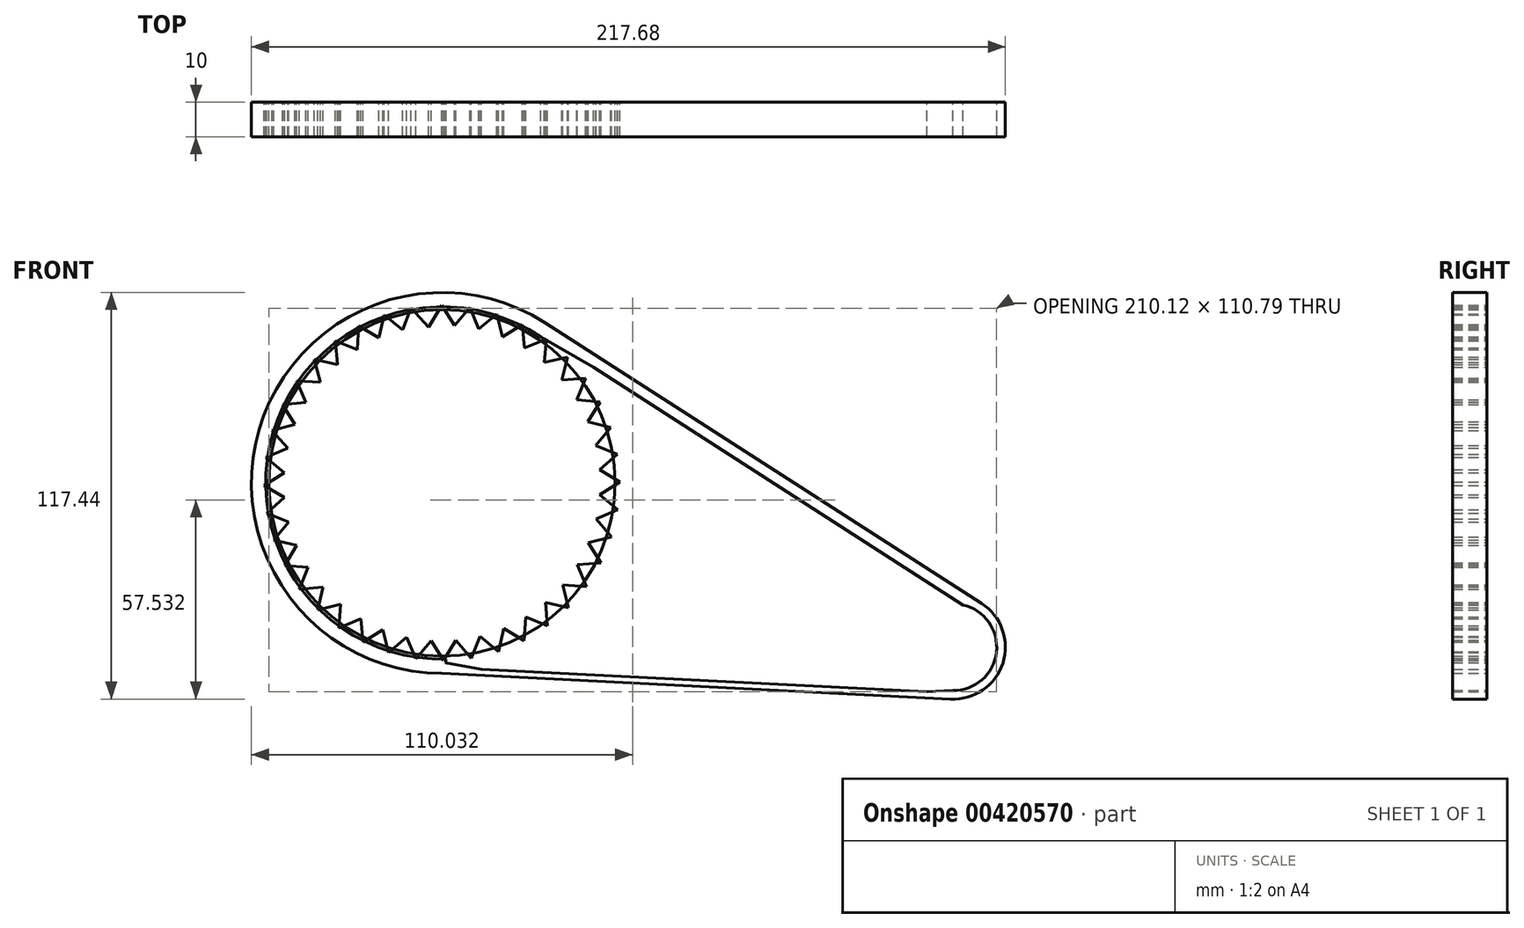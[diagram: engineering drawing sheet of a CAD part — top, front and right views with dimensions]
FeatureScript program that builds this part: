
annotation { "Feature Type Name" : "Feature", "Feature Type Description" : "" }
export const myFeature = defineFeature(function(context is Context, id is Id, definition is map)
    precondition{}
    {
        {
            var Q0;
            Q0=qCreatedBy(makeId("Front.planeOp"),FACE);
            var sketch = newSketch(context, id + "F0", { "sketchPlane" : qUnion([Q0])});
            skCircle(sketch, "E0", {"center": v(0, 0) * mm, "radius": 50 * mm});
            skSolve(sketch);
        }
        {
            var Q0;
            Q0=makeQuery(id+"F0.imprint","IMPRINT",FACE,{"disambiguationData":[TD([[makeQuery(id+"F0.imprint","IMPRINT",EDGE,{"derivedFrom":sQuery(id+"F0.wireOp",EDGE,"E0")}),1.0]])]});
            extrude(context, id + "F1", {"entities" : qUnion([Q0]), "depth" : 10 * mm});
        }
        {
            var Q0;
            Q0=qCreatedBy(makeId("Front.planeOp"),FACE);
            var sketch = newSketch(context, id + "F2", { "sketchPlane" : qUnion([Q0])});
            skCircle(sketch, "E1", {"center": v(147.68, -47.44) * mm, "radius": 12.5 * mm});
            skLineSegment(sketch, "E2", {"start": v(0, -55) * mm, "end": v(146.92, -62.42) * mm});
            skLineSegment(sketch, "E3", {"start": v(29.76, 46.26) * mm, "end": v(155.8, -34.82) * mm});
            skCircle(sketch, "E4", {"center": v(0, 0) * mm, "radius": 50.89 * mm});
            skLineSegment(sketch, "E5", {"start": v(29.76, 46.26) * mm, "end": v(0, -55) * mm});
            skCircle(sketch, "E6", {"center": v(0, 0) * mm, "radius": 55 * mm});
            skCircle(sketch, "E7", {"center": v(147.68, -47.44) * mm, "radius": 15 * mm});
            skLineSegment(sketch, "E8", {"start": v(43.69, 33.41) * mm, "end": v(146.17, -32.52) * mm});
            skLineSegment(sketch, "E9", {"start": v(139.96, -60.3) * mm, "end": v(11.38, -53.81) * mm});
            skLineSegment(sketch, "E10", {"start": v(43.69, 33.41) * mm, "end": v(28.58, 42.24) * mm});
            skLineSegment(sketch, "E11", {"start": v(11.38, -53.81) * mm, "end": v(0.91, -51.9) * mm});
            skLineSegment(sketch, "E12", {"start": v(146.17, -32.52) * mm, "end": v(150.4, -35.24) * mm});
            skLineSegment(sketch, "E13", {"start": v(139.96, -60.3) * mm, "end": v(149.06, -59.86) * mm});
            skSolve(sketch);
        }
        {
            var Q0;
            Q0 = qSketchRegion(id + "F2", true);
            extrude(context, id + "F3", {"entities" : qUnion([Q0]), "operationType" : NewBodyOperationType.ADD, "depth" : 10 * mm});
        }
        {
            var Q0;
            Q0=qCreatedBy(makeId("Front.planeOp"),FACE);
            var sketch = newSketch(context, id + "F4", { "sketchPlane" : qUnion([Q0])});
            skLineSegment(sketch, "E14", {"start": v(-4.25, 44.43) * mm, "end": v(0, 51.33) * mm});
            skLineSegment(sketch, "E15.MirrorCS", {"start": v(4.25, 44.43) * mm, "end": v(0, 51.33) * mm});
            skLineSegment(sketch, "E16.1.0", {"start": v(2.73, 44.54) * mm, "end": v(8, 50.7) * mm});
            skLineSegment(sketch, "E16.1.1", {"start": v(11.13, 43.22) * mm, "end": v(8, 50.7) * mm});
            skLineSegment(sketch, "E16.2.0", {"start": v(9.65, 43.57) * mm, "end": v(15.82, 48.83) * mm});
            skLineSegment(sketch, "E16.2.1", {"start": v(17.73, 40.95) * mm, "end": v(15.82, 48.83) * mm});
            skLineSegment(sketch, "E16.3.0", {"start": v(16.33, 41.53) * mm, "end": v(23.24, 45.77) * mm});
            skLineSegment(sketch, "E16.3.1", {"start": v(23.9, 37.69) * mm, "end": v(23.24, 45.77) * mm});
            skLineSegment(sketch, "E16.4.0", {"start": v(22.6, 38.48) * mm, "end": v(30.1, 41.58) * mm});
            skLineSegment(sketch, "E16.4.1", {"start": v(29.49, 33.5) * mm, "end": v(30.1, 41.58) * mm});
            skLineSegment(sketch, "E16.5.0", {"start": v(28.33, 34.48) * mm, "end": v(36.22, 36.38) * mm});
            skLineSegment(sketch, "E16.5.1", {"start": v(34.35, 28.49) * mm, "end": v(36.22, 36.38) * mm});
            skLineSegment(sketch, "E16.6.0", {"start": v(33.36, 29.64) * mm, "end": v(41.45, 30.28) * mm});
            skLineSegment(sketch, "E16.6.1", {"start": v(38.38, 22.78) * mm, "end": v(41.45, 30.28) * mm});
            skLineSegment(sketch, "E16.7.0", {"start": v(37.58, 24.07) * mm, "end": v(45.66, 23.45) * mm});
            skLineSegment(sketch, "E16.7.1", {"start": v(41.46, 16.51) * mm, "end": v(45.66, 23.45) * mm});
            skLineSegment(sketch, "E16.8.0", {"start": v(40.87, 17.92) * mm, "end": v(48.76, 16.04) * mm});
            skLineSegment(sketch, "E16.8.1", {"start": v(43.53, 9.84) * mm, "end": v(48.76, 16.04) * mm});
            skLineSegment(sketch, "E16.9.0", {"start": v(43.17, 11.32) * mm, "end": v(50.67, 8.23) * mm});
            skLineSegment(sketch, "E16.9.1", {"start": v(44.53, 2.93) * mm, "end": v(50.67, 8.23) * mm});
            skLineSegment(sketch, "E16.10.0", {"start": v(44.4, 4.45) * mm, "end": v(51.33, 0.23) * mm});
            skLineSegment(sketch, "E16.10.1", {"start": v(44.44, -4.05) * mm, "end": v(51.33, 0.23) * mm});
            skLineSegment(sketch, "E16.11.0", {"start": v(44.56, -2.53) * mm, "end": v(50.74, -7.78) * mm});
            skLineSegment(sketch, "E16.11.1", {"start": v(43.27, -10.93) * mm, "end": v(50.74, -7.78) * mm});
            skLineSegment(sketch, "E16.12.0", {"start": v(43.61, -9.45) * mm, "end": v(48.9, -15.6) * mm});
            skLineSegment(sketch, "E16.12.1", {"start": v(41.03, -17.55) * mm, "end": v(48.9, -15.6) * mm});
            skLineSegment(sketch, "E16.13.0", {"start": v(41.6, -16.14) * mm, "end": v(45.87, -23.04) * mm});
            skLineSegment(sketch, "E16.13.1", {"start": v(37.8, -23.73) * mm, "end": v(45.87, -23.04) * mm});
            skLineSegment(sketch, "E16.14.0", {"start": v(38.58, -22.43) * mm, "end": v(41.72, -29.91) * mm});
            skLineSegment(sketch, "E16.14.1", {"start": v(33.63, -29.34) * mm, "end": v(41.72, -29.91) * mm});
            skLineSegment(sketch, "E16.15.0", {"start": v(34.6, -28.18) * mm, "end": v(36.54, -36.05) * mm});
            skLineSegment(sketch, "E16.15.1", {"start": v(28.64, -34.23) * mm, "end": v(36.54, -36.05) * mm});
            skLineSegment(sketch, "E16.16.0", {"start": v(29.79, -33.23) * mm, "end": v(30.47, -41.31) * mm});
            skLineSegment(sketch, "E16.16.1", {"start": v(22.95, -38.27) * mm, "end": v(30.47, -41.31) * mm});
            skLineSegment(sketch, "E16.17.0", {"start": v(24.24, -37.47) * mm, "end": v(23.65, -45.56) * mm});
            skLineSegment(sketch, "E16.17.1", {"start": v(16.7, -41.39) * mm, "end": v(23.65, -45.56) * mm});
            skLineSegment(sketch, "E16.18.0", {"start": v(18.1, -40.8) * mm, "end": v(16.26, -48.69) * mm});
            skLineSegment(sketch, "E16.18.1", {"start": v(10.04, -43.48) * mm, "end": v(16.26, -48.69) * mm});
            skLineSegment(sketch, "E16.19.0", {"start": v(11.51, -43.12) * mm, "end": v(8.46, -50.63) * mm});
            skLineSegment(sketch, "E16.19.1", {"start": v(3.13, -44.52) * mm, "end": v(8.46, -50.63) * mm});
            skLineSegment(sketch, "E16.20.0", {"start": v(4.65, -44.39) * mm, "end": v(0.46, -51.33) * mm});
            skLineSegment(sketch, "E16.20.1", {"start": v(-3.85, -44.46) * mm, "end": v(0.46, -51.33) * mm});
            skLineSegment(sketch, "E16.21.0", {"start": v(-2.33, -44.57) * mm, "end": v(-7.55, -50.77) * mm});
            skLineSegment(sketch, "E16.21.1", {"start": v(-10.74, -43.32) * mm, "end": v(-7.55, -50.77) * mm});
            skLineSegment(sketch, "E16.22.0", {"start": v(-9.26, -43.66) * mm, "end": v(-15.38, -48.97) * mm});
            skLineSegment(sketch, "E16.22.1", {"start": v(-17.36, -41.11) * mm, "end": v(-15.38, -48.97) * mm});
            skLineSegment(sketch, "E16.23.0", {"start": v(-15.96, -41.68) * mm, "end": v(-22.83, -45.97) * mm});
            skLineSegment(sketch, "E16.23.1", {"start": v(-23.57, -37.9) * mm, "end": v(-22.83, -45.97) * mm});
            skLineSegment(sketch, "E16.24.0", {"start": v(-22.26, -38.68) * mm, "end": v(-29.72, -41.85) * mm});
            skLineSegment(sketch, "E16.24.1", {"start": v(-29.19, -33.76) * mm, "end": v(-29.72, -41.85) * mm});
            skLineSegment(sketch, "E16.25.0", {"start": v(-28.02, -34.73) * mm, "end": v(-35.89, -36.7) * mm});
            skLineSegment(sketch, "E16.25.1", {"start": v(-34.1, -28.8) * mm, "end": v(-35.89, -36.7) * mm});
            skLineSegment(sketch, "E16.26.0", {"start": v(-33.1, -29.94) * mm, "end": v(-41.17, -30.65) * mm});
            skLineSegment(sketch, "E16.26.1", {"start": v(-38.17, -23.12) * mm, "end": v(-41.17, -30.65) * mm});
            skLineSegment(sketch, "E16.27.0", {"start": v(-37.36, -24.4) * mm, "end": v(-45.45, -23.85) * mm});
            skLineSegment(sketch, "E16.27.1", {"start": v(-41.31, -16.88) * mm, "end": v(-45.45, -23.85) * mm});
            skLineSegment(sketch, "E16.28.0", {"start": v(-40.71, -18.28) * mm, "end": v(-48.62, -16.47) * mm});
            skLineSegment(sketch, "E16.28.1", {"start": v(-43.44, -10.23) * mm, "end": v(-48.62, -16.47) * mm});
            skLineSegment(sketch, "E16.29.0", {"start": v(-43.07, -11.7) * mm, "end": v(-50.6, -8.69) * mm});
            skLineSegment(sketch, "E16.29.1", {"start": v(-44.5, -3.33) * mm, "end": v(-50.6, -8.69) * mm});
            skLineSegment(sketch, "E16.30.0", {"start": v(-44.36, -4.84) * mm, "end": v(-51.33, -0.69) * mm});
            skLineSegment(sketch, "E16.30.1", {"start": v(-44.48, 3.65) * mm, "end": v(-51.33, -0.69) * mm});
            skLineSegment(sketch, "E16.31.0", {"start": v(-44.58, 2.14) * mm, "end": v(-50.8, 7.33) * mm});
            skLineSegment(sketch, "E16.31.1", {"start": v(-43.36, 10.55) * mm, "end": v(-50.8, 7.33) * mm});
            skLineSegment(sketch, "E16.32.0", {"start": v(-43.7, 9.06) * mm, "end": v(-49.04, 15.16) * mm});
            skLineSegment(sketch, "E16.32.1", {"start": v(-41.19, 17.18) * mm, "end": v(-49.04, 15.16) * mm});
            skLineSegment(sketch, "E16.33.0", {"start": v(-41.75, 15.77) * mm, "end": v(-46.08, 22.63) * mm});
            skLineSegment(sketch, "E16.33.1", {"start": v(-38, 23.4) * mm, "end": v(-46.08, 22.63) * mm});
            skLineSegment(sketch, "E16.34.0", {"start": v(-38.78, 22.09) * mm, "end": v(-41.98, 29.54) * mm});
            skLineSegment(sketch, "E16.34.1", {"start": v(-33.89, 29.04) * mm, "end": v(-41.98, 29.54) * mm});
            skLineSegment(sketch, "E16.35.0", {"start": v(-34.86, 27.87) * mm, "end": v(-36.86, 35.72) * mm});
            skLineSegment(sketch, "E16.35.1", {"start": v(-28.94, 33.97) * mm, "end": v(-36.86, 35.72) * mm});
            skLineSegment(sketch, "E16.36.0", {"start": v(-30.08, 32.96) * mm, "end": v(-30.84, 41.04) * mm});
            skLineSegment(sketch, "E16.36.1", {"start": v(-23.3, 38.07) * mm, "end": v(-30.84, 41.04) * mm});
            skLineSegment(sketch, "E16.37.0", {"start": v(-24.57, 37.25) * mm, "end": v(-24.06, 45.34) * mm});
            skLineSegment(sketch, "E16.37.1", {"start": v(-17.07, 41.23) * mm, "end": v(-24.06, 45.34) * mm});
            skLineSegment(sketch, "E16.38.0", {"start": v(-18.46, 40.63) * mm, "end": v(-16.7, 48.54) * mm});
            skLineSegment(sketch, "E16.38.1", {"start": v(-10.43, 43.4) * mm, "end": v(-16.7, 48.54) * mm});
            skLineSegment(sketch, "E16.39.0", {"start": v(-11.9, 43.01) * mm, "end": v(-8.91, 50.55) * mm});
            skLineSegment(sketch, "E16.39.1", {"start": v(-3.53, 44.49) * mm, "end": v(-8.91, 50.55) * mm});
            skPoint(sketch, "E16.center", {"position": v(0, 0) * mm});
            skLineSegment(sketch, "E16.anchor1", {"start": v(0, 0) * mm, "end": v(-4.25, 44.43) * mm, "construction": true});
            skLineSegment(sketch, "E16.anchor2", {"start": v(0, 0) * mm, "end": v(-11.9, 43.01) * mm, "construction": true});
            skSolve(sketch);
        }
        {
            var Q0;
            Q0 = qSketchRegion(id + "F4", true);
            extrude(context, id + "F5", {"entities" : qUnion([Q0]), "depth" : 10 * mm});
        }
    });
